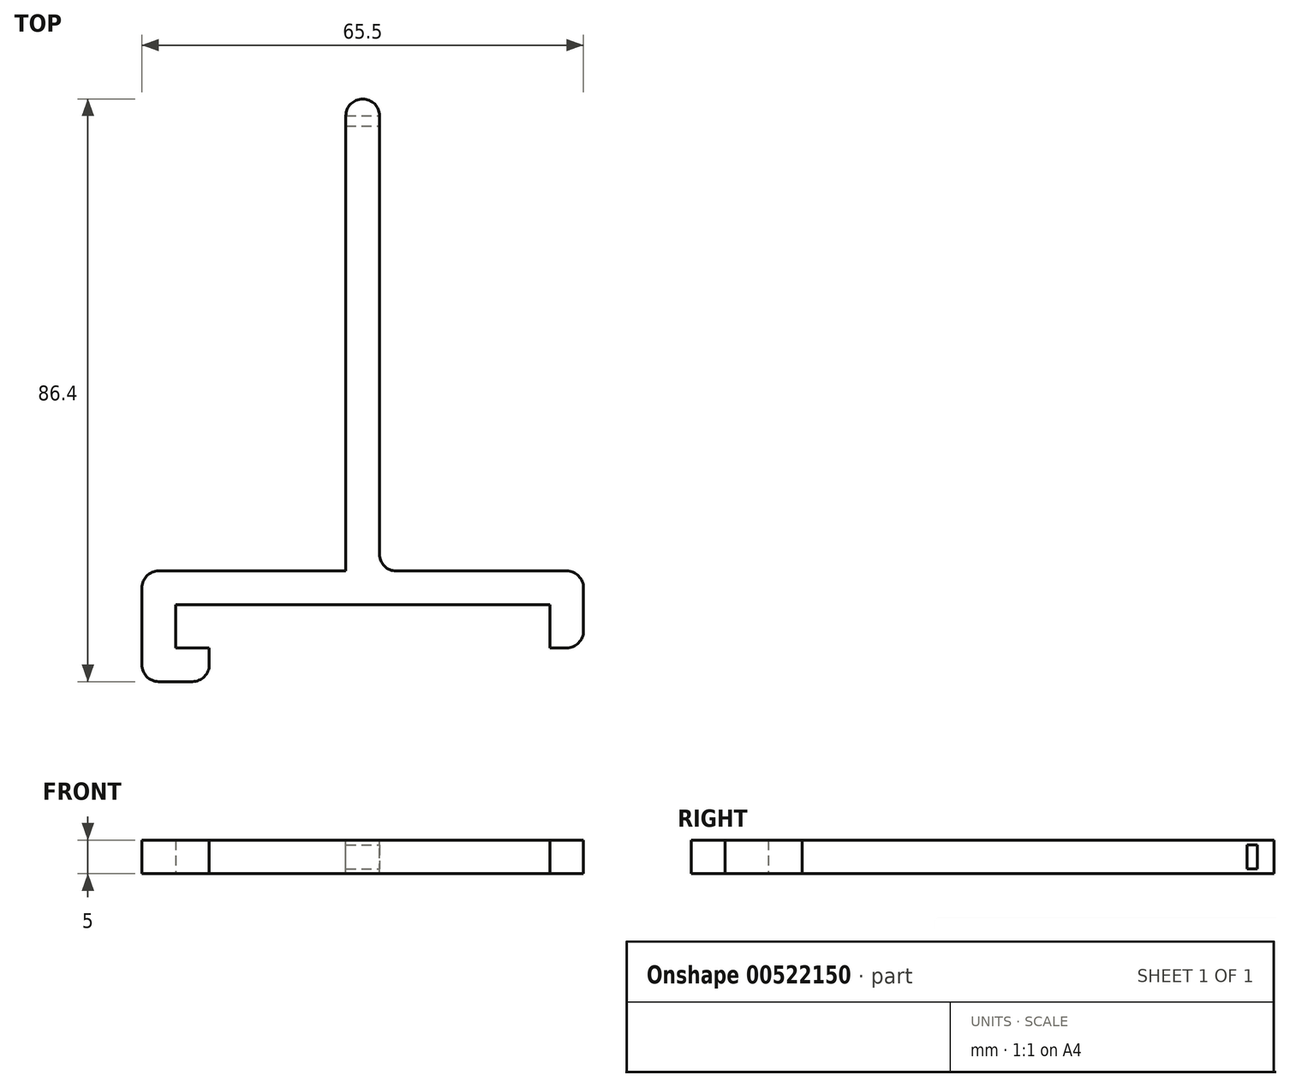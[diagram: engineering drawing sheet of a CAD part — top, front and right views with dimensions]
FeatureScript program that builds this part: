
annotation { "Feature Type Name" : "Feature", "Feature Type Description" : "" }
export const myFeature = defineFeature(function(context is Context, id is Id, definition is map)
    precondition{}
    {
        {
            var Q0;
            Q0=qCreatedBy(makeId("Top.planeOp"),FACE);
            var sketch = newSketch(context, id + "F0", { "sketchPlane" : qUnion([Q0])});
            skLineSegment(sketch, "E0.bottom", {"start": v(27.75, 3.2) * mm, "end": v(-27.75, 3.2) * mm});
            skLineSegment(sketch, "E0.top", {"start": v(27.75, -3.2) * mm, "end": v(-27.75, -3.2) * mm});
            skLineSegment(sketch, "E0.left", {"start": v(27.75, 3.2) * mm, "end": v(27.75, -3.2) * mm});
            skLineSegment(sketch, "E0.right", {"start": v(-27.75, 3.2) * mm, "end": v(-27.75, -3.2) * mm});
            skPoint(sketch, "E0.middle", {"position": v(0, 0) * mm});
            skLineSegment(sketch, "E1.bottom", {"start": v(27.75, -3.2) * mm, "end": v(32.75, -3.2) * mm});
            skLineSegment(sketch, "E1.top", {"start": v(27.75, 3.2) * mm, "end": v(32.75, 3.2) * mm});
            skLineSegment(sketch, "E1.left", {"start": v(27.75, -3.2) * mm, "end": v(27.75, 3.2) * mm});
            skLineSegment(sketch, "E1.right", {"start": v(32.75, -3.2) * mm, "end": v(32.75, 3.2) * mm});
            skLineSegment(sketch, "E2.bottom", {"start": v(-27.75, 8.2) * mm, "end": v(32.75, 8.2) * mm});
            skLineSegment(sketch, "E2.top", {"start": v(-27.75, 3.2) * mm, "end": v(32.75, 3.2) * mm});
            skLineSegment(sketch, "E2.left", {"start": v(-27.75, 8.2) * mm, "end": v(-27.75, 3.2) * mm});
            skLineSegment(sketch, "E2.right", {"start": v(32.75, 8.2) * mm, "end": v(32.75, 3.2) * mm});
            skLineSegment(sketch, "E3.bottom", {"start": v(-27.75, 8.2) * mm, "end": v(-32.75, 8.2) * mm});
            skLineSegment(sketch, "E3.top", {"start": v(-27.75, -3.2) * mm, "end": v(-32.75, -3.2) * mm});
            skLineSegment(sketch, "E3.left", {"start": v(-27.75, 8.2) * mm, "end": v(-27.75, -3.2) * mm});
            skLineSegment(sketch, "E3.right", {"start": v(-32.75, 8.2) * mm, "end": v(-32.75, -3.2) * mm});
            skLineSegment(sketch, "E4.bottom", {"start": v(-32.75, -3.2) * mm, "end": v(-22.75, -3.2) * mm});
            skLineSegment(sketch, "E4.top", {"start": v(-32.75, -8.2) * mm, "end": v(-22.75, -8.2) * mm});
            skLineSegment(sketch, "E4.left", {"start": v(-32.75, -3.2) * mm, "end": v(-32.75, -8.2) * mm});
            skLineSegment(sketch, "E4.right", {"start": v(-22.75, -3.2) * mm, "end": v(-22.75, -8.2) * mm});
            skSolve(sketch);
        }
        {
            var Q0;
            Q0=makeQuery(id+"F0.imprint","IMPRINT",FACE,{"disambiguationData":[TD([[makeQuery(id+"F0.imprint","IMPRINT",EDGE,{"derivedFrom":sQuery(id+"F0.wireOp",EDGE,"E1.bottom")}),1.0]])]});
            var Q1;
            {var subQ5=sQuery(id+"F0.wireOp",EDGE,"E2.bottom");Q1=makeQuery(id+"F0.imprint","IMPRINT",FACE,{"disambiguationData":[TD([[makeQuery(id+"F0.imprint","IMPRINT",EDGE,{"derivedFrom":subQ5}),-1.0]])]});}
            var Q2;
            {var subQ5=sQuery(id+"F0.wireOp",EDGE,"E3.bottom");Q2=makeQuery(id+"F0.imprint","IMPRINT",FACE,{"disambiguationData":[TD([[makeQuery(id+"F0.imprint","IMPRINT",EDGE,{"derivedFrom":subQ5}),1.0]])]});}
            var Q3;
            Q3=makeQuery(id+"F0.imprint","IMPRINT",FACE,{"disambiguationData":[TD([[makeQuery(id+"F0.imprint","IMPRINT",EDGE,{"derivedFrom":sQuery(id+"F0.wireOp",EDGE,"E4.top")}),1.0]])]});
            extrude(context, id + "F1", {"entities" : qUnion([Q0, Q1, Q2, Q3]), "depth" : 5 * mm, "offsetDistance" : 25 * mm});
        }
        {
            var Q0;
            Q0=makeQuery(id+"F1.opExtrude","SWEPT_FACE",FACE,{"disambiguationData":[OSD([sQuery(id+"F0.wireOp",EDGE,"E2.bottom"),sQuery(id+"F0.wireOp",EDGE,"E3.bottom")])]});
            var sketch = newSketch(context, id + "F2", { "sketchPlane" : qUnion([Q0])});
            skLineSegment(sketch, "E5.bottom", {"start": v(-2.5, 0) * mm, "end": v(2.5, 0) * mm});
            skLineSegment(sketch, "E5.top", {"start": v(-2.5, 5) * mm, "end": v(2.5, 5) * mm});
            skLineSegment(sketch, "E5.left", {"start": v(-2.5, 0) * mm, "end": v(-2.5, 5) * mm});
            skLineSegment(sketch, "E5.right", {"start": v(2.5, 0) * mm, "end": v(2.5, 5) * mm});
            skPoint(sketch, "E6", {"position": v(0, 0) * mm});
            skSolve(sketch);
        }
        {
            var Q0;
            Q0=makeQuery(id+"F2.imprint","IMPRINT",FACE,{"disambiguationData":[TD([[makeQuery(id+"F2.imprint","IMPRINT",EDGE,{"derivedFrom":sQuery(id+"F2.wireOp",EDGE,"E5.bottom")}),-1.0]])]});
            extrude(context, id + "F3", {"entities" : qUnion([Q0]), "operationType" : NewBodyOperationType.ADD, "depth" : 70 * mm, "offsetDistance" : 25 * mm});
        }
        {
            var Q0;
            Q0=makeQuery(id+"F3.opExtrude","SWEPT_FACE",FACE,{"disambiguationData":[OSD([sQuery(id+"F2.wireOp",EDGE,"E5.left")])]});
            var sketch = newSketch(context, id + "F4", { "sketchPlane" : qUnion([Q0])});
            skLineSegment(sketch, "E7", {"start": v(78.2, 2.5) * mm, "end": v(75.7, 2.5) * mm, "construction": true});
            skLineSegment(sketch, "E8.bottom", {"start": v(74.2, 4.25) * mm, "end": v(75.7, 4.25) * mm});
            skLineSegment(sketch, "E8.top", {"start": v(74.2, 0.75) * mm, "end": v(75.7, 0.75) * mm});
            skLineSegment(sketch, "E8.left", {"start": v(74.2, 4.25) * mm, "end": v(74.2, 0.75) * mm});
            skLineSegment(sketch, "E8.right", {"start": v(75.7, 4.25) * mm, "end": v(75.7, 0.75) * mm});
            skPoint(sketch, "E9", {"position": v(75.7, 2.5) * mm});
            skSolve(sketch);
        }
        {
            var Q0;
            Q0=makeQuery(id+"F4.imprint","IMPRINT",FACE,{"disambiguationData":[TD([[makeQuery(id+"F4.imprint","IMPRINT",EDGE,{"derivedFrom":sQuery(id+"F4.wireOp",EDGE,"E8.bottom")}),-1.0]])]});
            extrude(context, id + "F5", {"entities" : qUnion([Q0]), "operationType" : NewBodyOperationType.REMOVE, "endBound" : BoundingType.UP_TO_NEXT, "oppositeDirection" : true, "depth" : 25 * mm, "offsetDistance" : 25 * mm});
        }
        {
            var Q0;
            Q0=makeQuery(id+"F1.opExtrude","SWEPT_EDGE",EDGE,{"disambiguationData":[OSD([sQuery(id+"F0.wireOp",EDGE,"E2.bottom"),sQuery(id+"F0.wireOp",EDGE,"E2.right")])]});
            var Q1;
            Q1=makeQuery(id+"F3.opExtrude","CAP_EDGE",EDGE,{"disambiguationData":[OSD([sQuery(id+"F2.wireOp",EDGE,"E5.left")])],"isStart":true});
            var Q2;
            Q2=makeQuery(id+"F3.opExtrude","CAP_EDGE",EDGE,{"disambiguationData":[OSD([sQuery(id+"F2.wireOp",EDGE,"E5.right")])],"isStart":true});
            var Q3;
            Q3=makeQuery(id+"F1.opExtrude","SWEPT_EDGE",EDGE,{"disambiguationData":[OSD([sQuery(id+"F0.wireOp",EDGE,"E3.bottom"),sQuery(id+"F0.wireOp",EDGE,"E3.right")])]});
            var Q4;
            Q4=makeQuery(id+"F1.opExtrude","SWEPT_EDGE",EDGE,{"disambiguationData":[OSD([sQuery(id+"F0.wireOp",EDGE,"E1.bottom"),sQuery(id+"F0.wireOp",EDGE,"E1.right")])]});
            var Q5;
            Q5=makeQuery(id+"F1.opExtrude","SWEPT_EDGE",EDGE,{"disambiguationData":[OSD([sQuery(id+"F0.wireOp",EDGE,"E4.top"),sQuery(id+"F0.wireOp",EDGE,"E4.left")])]});
            var Q6;
            Q6=makeQuery(id+"F1.opExtrude","SWEPT_EDGE",EDGE,{"disambiguationData":[OSD([sQuery(id+"F0.wireOp",EDGE,"E4.top"),sQuery(id+"F0.wireOp",EDGE,"E4.right")])]});
            var Q7;
            Q7=makeQuery(id+"F3.opExtrude","CAP_EDGE",EDGE,{"disambiguationData":[OSD([sQuery(id+"F2.wireOp",EDGE,"E5.right")])],"isStart":false});
            var Q8;
            Q8=makeQuery(id+"F3.opExtrude","CAP_EDGE",EDGE,{"disambiguationData":[OSD([sQuery(id+"F2.wireOp",EDGE,"E5.left")])],"isStart":false});
            fillet(context, id + "F6", {"entities" : qUnion([Q0, Q1, Q2, Q3, Q4, Q5, Q6, Q7, Q8]), "radius" : 2.5 * mm, "tangentPropagation" : true, "allowEdgeOverflow" : false});
        }
    });
